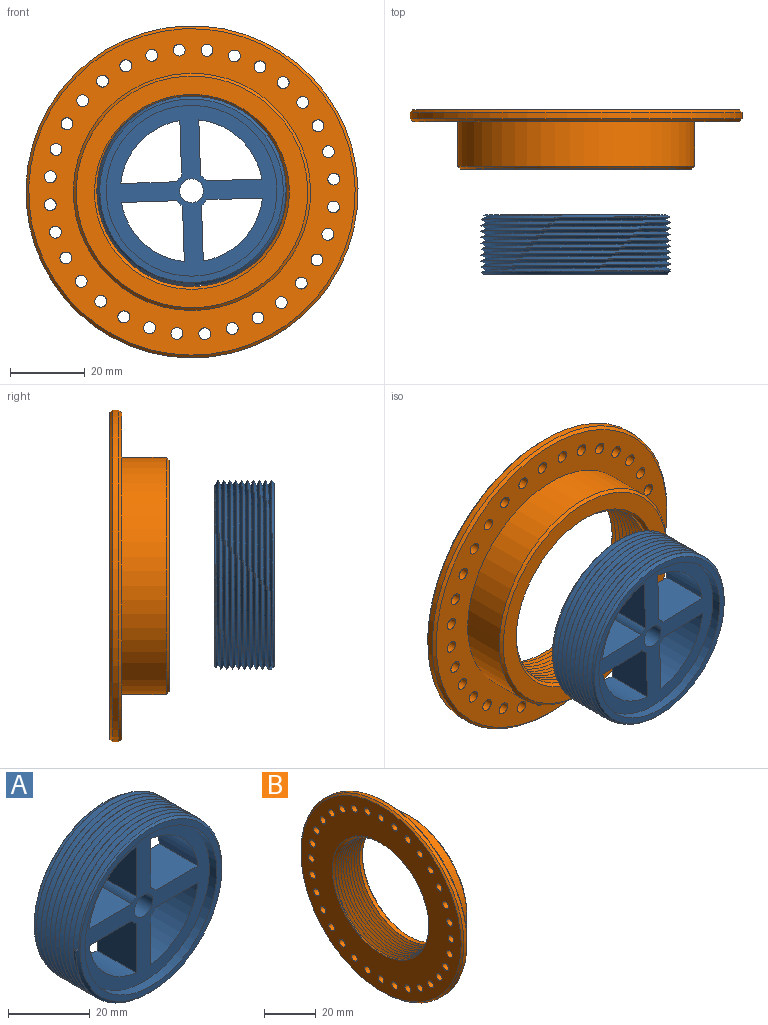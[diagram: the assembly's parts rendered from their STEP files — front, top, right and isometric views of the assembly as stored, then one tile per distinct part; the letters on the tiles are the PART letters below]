
ASSEMBLY  parts=2 mates=1
PART A: 27 faces, bbox 51x17.3x58.9 mm
  f0: cylinder r=19.05mm len=16.34mm, axis (0,1,0), area 331.1mm2, adj f1,f12,f20,f26
  f1: plane 14.85x13.34mm, normal (0,0,1), area 198mm2, adj f0,f2,f20,f26
  f2: cylinder r=4.76mm len=13.34mm, axis (0,1,0), area 28.3mm2, adj f1,f12,f20,f26
  f3: cylinder r=19.05mm len=16.34mm, axis (0,1,0), area 331.1mm2, adj f4,f13,f20,f26
  f4: plane 14.85x13.34mm, normal (1,0,0), area 198mm2, adj f3,f5,f20,f26
  f5: cylinder r=4.76mm len=13.34mm, axis (0,1,0), area 28.3mm2, adj f4,f13,f20,f26
  f6: cylinder r=19.05mm len=16.34mm, axis (0,1,0), area 331.1mm2, adj f7,f14,f20,f26
  f7: plane 14.85x13.34mm, normal (0,0,-1), area 198mm2, adj f6,f8,f20,f26
  f8: cylinder r=4.76mm len=13.34mm, axis (0,1,0), area 28.3mm2, adj f7,f14,f20,f26
  f9: cylinder r=19.05mm len=16.34mm, axis (0,1,0), area 331.1mm2, adj f10,f15,f20,f26
  f10: plane 14.85x13.34mm, normal (-1,0,0), area 198mm2, adj f9,f11,f20,f26
  f11: cylinder r=4.76mm len=13.34mm, axis (0,1,0), area 28.3mm2, adj f10,f15,f20,f26
  f12: plane 14.85x13.34mm, normal (1,0,0), area 198mm2, adj f0,f2,f20,f26
  f13: plane 14.85x13.34mm, normal (0,0,-1), area 198mm2, adj f3,f5,f20,f26
  f14: plane 14.85x13.34mm, normal (-1,0,0), area 198mm2, adj f6,f8,f20,f26
  f15: plane 14.85x13.34mm, normal (0,0,1), area 198mm2, adj f9,f11,f20,f26
  f16: cylinder r=3.17mm len=13.34mm, axis (0,1,0), area 266mm2, adj f20,f26
  f17: cylinder r=25.32mm len=50.64mm, axis (0,1,0), area -13.6mm2, adj f18,f21,f22,f23,f24
  f18: cone r=24.56mm half-angle=45deg, axis (0,1,0), area 143mm2, adj f17,f19,f23,f24
  f19: plane 49.12x49.12mm, normal (0,-1,0), area 252.9mm2, adj f18,f25
  f20: plane 49.52x48.94mm, normal (0,1,0), area 1067.9mm2, adj f0,f1,f2,f3,f4,f5,f6,f7
  f21: cone r=25.32mm half-angle=45deg, axis (0,-1,0), area 47.7mm2, adj f17,f20,f22,f23
  f22: bspline ~58.47x50.64mm, area 2221.1mm2, adj f17,f20,f21,f23,f24
  f23: bspline ~58.47x50.64mm, area 2329.4mm2, adj f17,f18,f20,f21,f22,f24
  f24: plane 1.36x1.3mm, normal (0,0,1), area 0.9mm2, adj f17,f18,f22,f23
  f25: cylinder r=22.86mm len=45.72mm, axis (0,-1,0), area 364.8mm2, adj f19,f26
  f26: plane 45.72x45.72mm, normal (0,-1,0), area 835.2mm2, adj f0,f1,f2,f3,f4,f5,f6,f7
PART B: 47 faces, bbox 17.2x89.4x89.4 mm
  f0: cylinder r=25.32mm len=50.65mm, axis (-1,0,0), area 235.4mm2, adj f42,f45,f46
  f1: cylinder r=1.59mm len=3.18mm, axis (-1,0,0), area 31.7mm2, adj f34,f35
  f2: cylinder r=1.59mm len=3.18mm, axis (-1,0,0), area 31.7mm2, adj f34,f35
  f3: cylinder r=1.59mm len=3.18mm, axis (-1,0,0), area 31.7mm2, adj f34,f35
  f4: cylinder r=1.59mm len=3.18mm, axis (-1,0,0), area 31.7mm2, adj f34,f35
  f5: cylinder r=1.59mm len=3.18mm, axis (-1,0,0), area 31.7mm2, adj f34,f35
  f6: cylinder r=1.59mm len=3.18mm, axis (-1,0,0), area 31.7mm2, adj f34,f35
  f7: cylinder r=1.59mm len=3.18mm, axis (-1,0,0), area 31.7mm2, adj f34,f35
  f8: cylinder r=1.59mm len=3.18mm, axis (-1,0,0), area 31.7mm2, adj f34,f35
  f9: cylinder r=1.59mm len=3.18mm, axis (-1,0,0), area 31.7mm2, adj f34,f35
  f10: cylinder r=1.59mm len=3.18mm, axis (-1,0,0), area 31.7mm2, adj f34,f35
  f11: cylinder r=1.59mm len=3.18mm, axis (-1,0,0), area 31.7mm2, adj f34,f35
  f12: cylinder r=1.59mm len=3.18mm, axis (-1,0,0), area 31.7mm2, adj f34,f35
  f13: cylinder r=1.59mm len=3.18mm, axis (-1,0,0), area 31.7mm2, adj f34,f35
  f14: cylinder r=1.59mm len=3.18mm, axis (-1,0,0), area 31.7mm2, adj f34,f35
  f15: cylinder r=1.59mm len=3.18mm, axis (-1,0,0), area 31.7mm2, adj f34,f35
  f16: cylinder r=1.59mm len=3.18mm, axis (-1,0,0), area 31.7mm2, adj f34,f35
  f17: cylinder r=1.59mm len=3.18mm, axis (-1,0,0), area 31.7mm2, adj f34,f35
  f18: cylinder r=1.59mm len=3.18mm, axis (-1,0,0), area 31.7mm2, adj f34,f35
  f19: cylinder r=1.59mm len=3.18mm, axis (-1,0,0), area 31.7mm2, adj f34,f35
  f20: cylinder r=1.59mm len=3.18mm, axis (-1,0,0), area 31.7mm2, adj f34,f35
  f21: cylinder r=1.59mm len=3.18mm, axis (-1,0,0), area 31.7mm2, adj f34,f35
  f22: cylinder r=1.59mm len=3.18mm, axis (-1,0,0), area 31.7mm2, adj f34,f35
  f23: cylinder r=1.59mm len=3.18mm, axis (-1,0,0), area 31.7mm2, adj f34,f35
  f24: cylinder r=1.59mm len=3.18mm, axis (-1,0,0), area 31.7mm2, adj f34,f35
  f25: cylinder r=1.59mm len=3.18mm, axis (-1,0,0), area 31.7mm2, adj f34,f35
  f26: cylinder r=1.59mm len=3.18mm, axis (-1,0,0), area 31.7mm2, adj f34,f35
  f27: cylinder r=1.59mm len=3.18mm, axis (-1,0,0), area 31.7mm2, adj f34,f35
  f28: cylinder r=1.59mm len=3.18mm, axis (-1,0,0), area 31.7mm2, adj f34,f35
  f29: cylinder r=1.59mm len=3.18mm, axis (-1,0,0), area 31.7mm2, adj f34,f35
  f30: cylinder r=1.59mm len=3.18mm, axis (-1,0,0), area 31.7mm2, adj f34,f35
  f31: cylinder r=1.59mm len=3.18mm, axis (-1,0,0), area 31.7mm2, adj f34,f35
  f32: cylinder r=1.59mm len=3.18mm, axis (-1,0,0), area 31.7mm2, adj f34,f35
  f33: cylinder r=44.45mm len=88.9mm, axis (-1,0,0), area 461.1mm2, adj f39,f40
  f34: plane 87.38x87.38mm, normal (1,0,0), area 2575.9mm2, adj f1,f2,f3,f4,f5,f6,f7,f8
  f35: plane 87.91x87.91mm, normal (-1,0,0), area 3582.8mm2, adj f1,f2,f3,f4,f5,f6,f7,f8
  f36: cylinder r=31.75mm len=63.5mm, axis (-1,0,0), area 2381.5mm2, adj f34,f41
  f37: plane 61.98x61.98mm, normal (1,0,0), area 879mm2, adj f41,f42
  f38: cone r=26.09mm half-angle=45deg, axis (-1,0,0), area 40.6mm2, adj f35,f43,f44
  f39: cone r=44.45mm half-angle=45deg, axis (1,0,0), area 298.4mm2, adj f33,f35
  f40: cone r=43.69mm half-angle=45deg, axis (-1,0,0), area 298.4mm2, adj f33,f34
  f41: cone r=30.99mm half-angle=45deg, axis (-1,0,0), area 212.4mm2, adj f36,f37
  f42: cone r=25.32mm half-angle=45deg, axis (1,0,0), area 174mm2, adj f0,f37
  f43: bspline ~61.58x53.33mm, area 2127.5mm2, adj f35,f38,f44,f45
  f44: bspline ~61.58x53.33mm, area 2245.7mm2, adj f35,f38,f43,f45,f46
  f45: plane 1.49x1.34mm, normal (0,0,1), area 1mm2, adj f0,f43,f44,f46
  f46: bspline ~58.71x50.85mm, area 18.2mm2, adj f0,f44,f45
PLACE A rot(axis=(0,-1,0),91.8deg) t=(-33.72,-0.27,25.49)mm
PLACE B rot(axis=(0.23,-0.23,-0.94),93.3deg) t=(-33.61,27.89,25.19)mm
MATE cylindrical A.f20 <-> B.f35  axis (0,1,0) through (-33.71,-0.27,25.1)mm
